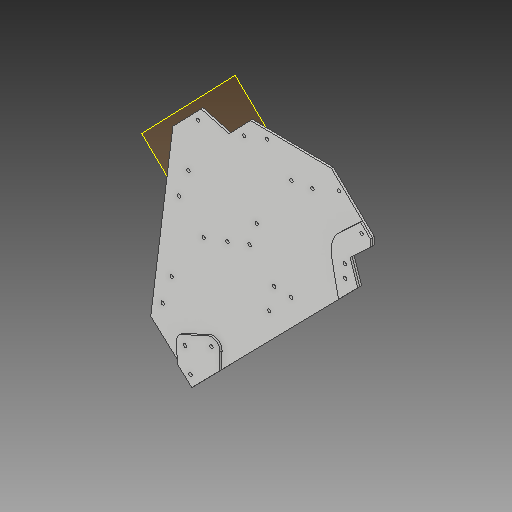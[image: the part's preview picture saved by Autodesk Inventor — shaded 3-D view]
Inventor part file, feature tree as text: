
AUTODESK INVENTOR PART (.ipt)
format: ipt  version: 2019.2 (Build 232265000, 265)  size: 208,384 bytes
history: native  units: mm
features: other x21, reference x21, extrude x3, sketch x3, plane x1, chamfer x1, fillet x1
ambient origin geometry x8: Origin, YZ Plane, XZ Plane, XY Plane, X Axis, Y Axis, Z Axis, Center Point
bodies: Body1 (feature_tree), Body2 (feature_tree), Body3 (feature_tree)
feature tree (51):
  other  "SidePlate"
  plane  "Work Plane1"
  extrude  "Extrusion1"  Depth=3.0mm TaperAngle=45.0deg
  chamfer  "Chamfer1"  Distance=5.0mm
  extrude  "Extrusion2"  Depth=10.0mm
  extrude  "Extrusion3"  Depth=10.0mm
  fillet  "Fillet1"  Radius=3.0mm
  sketch  "Sketch1"  dims[d0=3.0mm d1=0.0mm d2=8.0mm d3=2.0mm d4=45.0deg]
  reference  "Reference1"
  reference  "Reference2"
  reference  "Reference3"
  reference  "Reference4"
  reference  "Reference5"
  reference  "Reference6"
  reference  "Reference7"
  reference  "Reference8"
  reference  "Reference9"
  reference  "Reference10"
  reference  "Reference11"
  reference  "Reference12"
  reference  "Reference13"
  reference  "Reference14"
  reference  "Reference15"
  reference  "Reference16"
  reference  "Reference17"
  reference  "Reference18"
  reference  "Reference19"
  reference  "Reference20"
  sketch  "Sketch2"  dims[d5=5.0mm]
  other  "ReinforcementRear"
  sketch  "Sketch3"  dims[d6=5.0mm d7=5.0mm d8=10.0mm d9=10.0mm d10=3.0mm d11=0.0mm d12=3.0mm d13=0.0mm d14=38.75mm]
  reference  "Reference21"
  other  "ReinforcementFront"
  other  "<userpath>\Desktop\3dprojects\OpenEmoto\MainFrame\Battery\Assembly.iam"
  other  "Assembly.iam"
  other  "BatteryArrangement:1"
  other  "SpacerBig:2"
  other  "SpacerSmall:3"
  other  "SpacerBig:1"
  other  "SpacerSmall:4"
  other  "SpacerBig:4"
  other  "SpacerSmall:5"
  other  "SpacerBig:5"
  other  "SpacerSmall:2"
  other  "SpacerSmall:6"
  other  "SpacerBig:6"
  other  "LowerCage:1"
  other  "<userpath>\Desktop\3dprojects\OpenEmoto\MainFrame\Battery\Assembly2.iam"
  other  "Assembly2.iam"
  other  "BatteryArrangement1:1"
  other  "Multistar-6S-16Ah:2"
